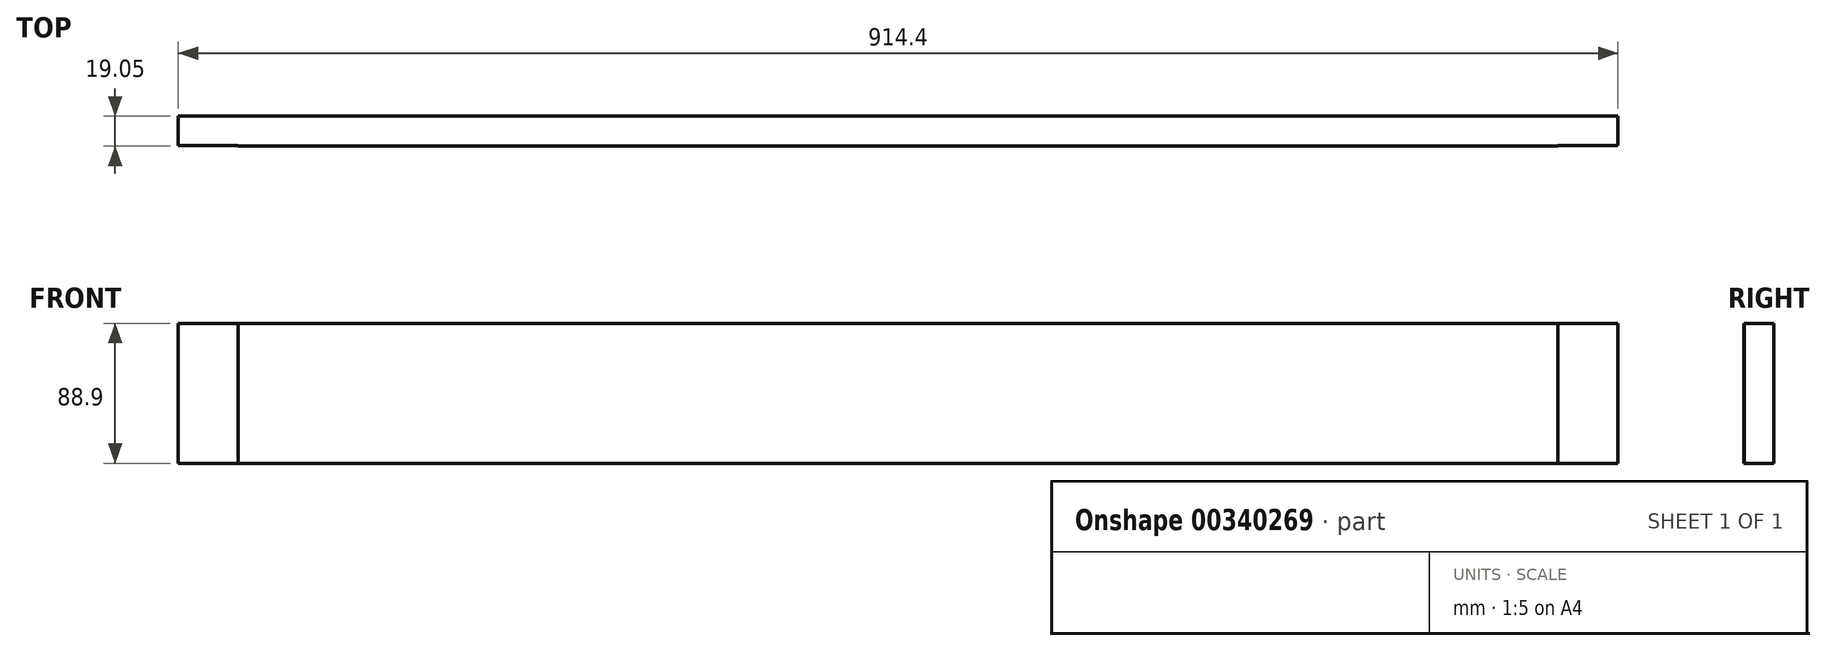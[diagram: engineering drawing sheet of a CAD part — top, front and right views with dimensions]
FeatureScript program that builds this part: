
annotation { "Feature Type Name" : "Feature", "Feature Type Description" : "" }
export const myFeature = defineFeature(function(context is Context, id is Id, definition is map)
    precondition{}
    {
        {
            var Q0;
            Q0=qCreatedBy(makeId("Front.planeOp"),FACE);
            var sketch = newSketch(context, id + "F0", { "sketchPlane" : qUnion([Q0])});
            skLineSegment(sketch, "E0.bottom", {"start": v(457.2, -44.45) * mm, "end": v(-457.2, -44.45) * mm});
            skLineSegment(sketch, "E0.top", {"start": v(457.2, 44.45) * mm, "end": v(-457.2, 44.45) * mm});
            skLineSegment(sketch, "E0.left", {"start": v(457.2, -44.45) * mm, "end": v(457.2, 44.45) * mm});
            skLineSegment(sketch, "E0.right", {"start": v(-457.2, -44.45) * mm, "end": v(-457.2, 44.45) * mm});
            skPoint(sketch, "E0.middle", {"position": v(0, 0) * mm});
            skSolve(sketch);
        }
        {
            var Q0;
            Q0 = qSketchRegion(id + "F0", true);
            extrude(context, id + "F1", {"entities" : qUnion([Q0]), "depth" : 19.05 * mm});
        }
        {
            var Q0;
            Q0=makeQuery(id+"F1.opExtrude","CAP_FACE",FACE,{"disambiguationData":[OSD([sQuery(id+"F0.wireOp",EDGE,"E0.bottom"),sQuery(id+"F0.wireOp",EDGE,"E0.top"),sQuery(id+"F0.wireOp",EDGE,"E0.left"),sQuery(id+"F0.wireOp",EDGE,"E0.right")])],"isStart":false});
            var sketch = newSketch(context, id + "F2", { "sketchPlane" : qUnion([Q0])});
            skLineSegment(sketch, "E1.bottom", {"start": v(-457.2, 44.45) * mm, "end": v(-419.1, 44.45) * mm});
            skLineSegment(sketch, "E1.top", {"start": v(-457.2, -44.45) * mm, "end": v(-419.1, -44.45) * mm});
            skLineSegment(sketch, "E1.left", {"start": v(-457.2, 44.45) * mm, "end": v(-457.2, -44.45) * mm});
            skLineSegment(sketch, "E1.right", {"start": v(-419.1, 44.45) * mm, "end": v(-419.1, -44.45) * mm});
            skLineSegment(sketch, "E2", {"start": v(0, 44.45) * mm, "end": v(0, -44.45) * mm, "construction": true});
            skLineSegment(sketch, "E3.MirrorCS", {"start": v(419.1, 44.45) * mm, "end": v(419.1, -44.45) * mm});
            skLineSegment(sketch, "E4.MirrorCS", {"start": v(457.2, 44.45) * mm, "end": v(457.2, -44.45) * mm});
            skLineSegment(sketch, "E5.MirrorCS", {"start": v(457.2, -44.45) * mm, "end": v(419.1, -44.45) * mm});
            skLineSegment(sketch, "E6.MirrorCS", {"start": v(457.2, 44.45) * mm, "end": v(419.1, 44.45) * mm});
            skSolve(sketch);
        }
        {
            var Q0;
            Q0 = qSketchRegion(id + "F2", true);
            extrude(context, id + "F3", {"entities" : qUnion([Q0]), "operationType" : NewBodyOperationType.REMOVE, "oppositeDirection" : true, "depth" : ((3 / 4) / 2) * mm});
        }
    });
